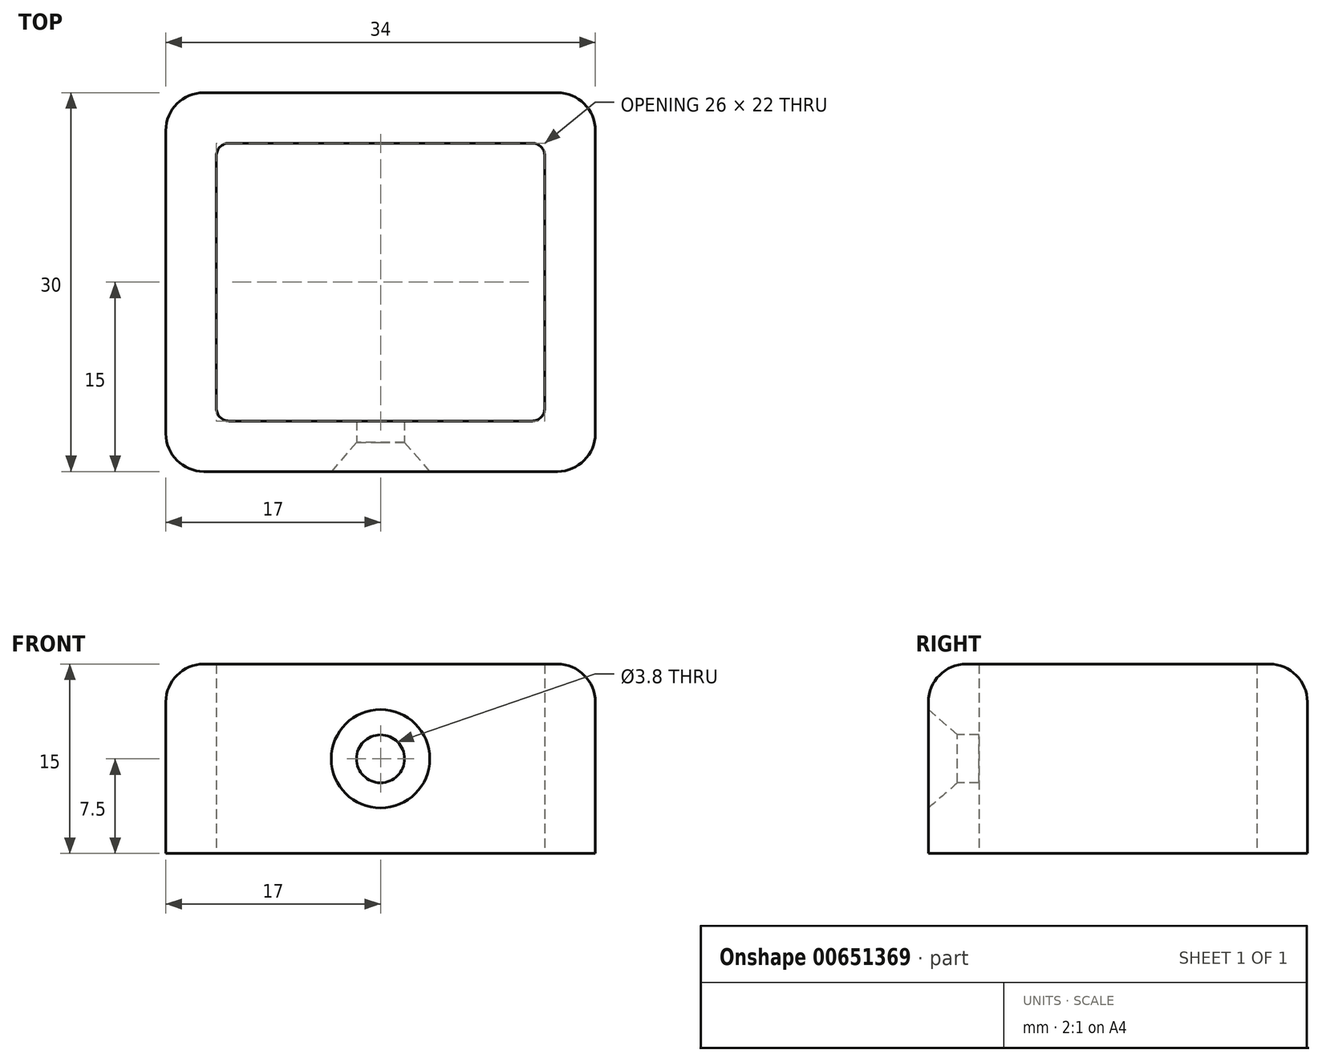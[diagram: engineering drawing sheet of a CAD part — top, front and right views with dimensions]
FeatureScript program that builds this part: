
annotation { "Feature Type Name" : "Feature", "Feature Type Description" : "" }
export const myFeature = defineFeature(function(context is Context, id is Id, definition is map)
    precondition{}
    {
        {
            var Q0;
            Q0=qCreatedBy(makeId("Top.planeOp"),FACE);
            var sketch = newSketch(context, id + "F0", { "sketchPlane" : qUnion([Q0])});
            skLineSegment(sketch, "E0.bottom", {"start": v(13, -11) * mm, "end": v(-13, -11) * mm});
            skLineSegment(sketch, "E0.top", {"start": v(13, 11) * mm, "end": v(-13, 11) * mm});
            skLineSegment(sketch, "E0.left", {"start": v(13, -11) * mm, "end": v(13, 11) * mm});
            skLineSegment(sketch, "E0.right", {"start": v(-13, -11) * mm, "end": v(-13, 11) * mm});
            skPoint(sketch, "E0.middle", {"position": v(0, 0) * mm});
            skLineSegment(sketch, "E1.0", {"start": v(17, 15) * mm, "end": v(-17, 15) * mm});
            skLineSegment(sketch, "E1.1", {"start": v(17, -15) * mm, "end": v(17, 15) * mm});
            skLineSegment(sketch, "E1.2", {"start": v(17, -15) * mm, "end": v(-17, -15) * mm});
            skLineSegment(sketch, "E1.3", {"start": v(-17, -15) * mm, "end": v(-17, 15) * mm});
            skSolve(sketch);
        }
        {
            var Q0;
            Q0=makeQuery(id+"F0.imprint","IMPRINT",FACE,{"disambiguationData":[TD([[makeQuery(id+"F0.imprint","IMPRINT",EDGE,{"derivedFrom":sQuery(id+"F0.wireOp",EDGE,"E0.bottom")}),1.0]])]});
            extrude(context, id + "F1", {"entities" : qUnion([Q0]), "depth" : 15 * mm, "offsetDistance" : 25 * mm});
        }
        {
            var Q0;
            Q0=makeQuery(id+"F1.opExtrude","SWEPT_FACE",FACE,{"disambiguationData":[OSD([sQuery(id+"F0.wireOp",EDGE,"E1.2")])]});
            var sketch = newSketch(context, id + "F2", { "sketchPlane" : qUnion([Q0])});
            skPoint(sketch, "E2", {"position": v(0, 7.5) * mm});
            skPoint(sketch, "E2.positionSnap0", {"position": v(-17, 7.5) * mm});
            skPoint(sketch, "E2.positionSnap1", {"position": v(0, 15) * mm});
            skSolve(sketch);
        }
        {
            var Q0;
            Q0=sQuery(id+"F2.wireOp",VERTEX,"E2");
            var Q1;
            Q1=makeQuery(id+"F1.opExtrude","SWEPT_BODY",BODY,{"disambiguationData":[OSD([sQuery(id+"F0.wireOp",EDGE,"E0.bottom"),sQuery(id+"F0.wireOp",EDGE,"E0.top"),sQuery(id+"F0.wireOp",EDGE,"E0.left"),sQuery(id+"F0.wireOp",EDGE,"E0.right"),sQuery(id+"F0.wireOp",EDGE,"E1.0"),sQuery(id+"F0.wireOp",EDGE,"E1.1"),sQuery(id+"F0.wireOp",EDGE,"E1.2"),sQuery(id+"F0.wireOp",EDGE,"E1.3")])]});
            hole(context, id + "F3", {"style" : HoleStyle.C_SINK, "endStyle" : HoleEndStyle.BLIND, "standardTappedOrClearance" : lookupTablePath({ "standard" : "ANSI", "fit" : "Normal (ASME)", "size" : "#6", "type" : "Clearance" }), "standardBlindInLast" : lookupTablePath({ "fit" : "Free", "standard" : "ANSI", "size" : "#6", "type" : "Clearance" }), "holeDiameter" : 3.8 * mm, "cSinkDiameter" : 7.8 * mm, "cSinkAngle" : 82 * degree, "majorDiameter" : 3.5 * mm, "holeDepth" : 5 * mm, "isTappedThrough" : true, "tappedDepth" : 3.8 * mm, "tapClearance" : 0, "locations" : qUnion([Q0]), "scope" : qUnion([Q1])});
        }
        {
            var Q0;
            Q0=makeQuery(id+"F1.opExtrude","SWEPT_EDGE",EDGE,{"disambiguationData":[OSD([sQuery(id+"F0.wireOp",EDGE,"E1.2"),sQuery(id+"F0.wireOp",EDGE,"E1.3")])]});
            var Q1;
            Q1=makeQuery(id+"F1.opExtrude","SWEPT_EDGE",EDGE,{"disambiguationData":[OSD([sQuery(id+"F0.wireOp",EDGE,"E1.1"),sQuery(id+"F0.wireOp",EDGE,"E1.2")])]});
            var Q2;
            Q2=makeQuery(id+"F1.opExtrude","SWEPT_EDGE",EDGE,{"disambiguationData":[OSD([sQuery(id+"F0.wireOp",EDGE,"E1.0"),sQuery(id+"F0.wireOp",EDGE,"E1.1")])]});
            var Q3;
            Q3=makeQuery(id+"F1.opExtrude","SWEPT_EDGE",EDGE,{"disambiguationData":[OSD([sQuery(id+"F0.wireOp",EDGE,"E1.0"),sQuery(id+"F0.wireOp",EDGE,"E1.3")])]});
            var Q4;
            Q4=makeQuery(id+"F1.opExtrude","CAP_EDGE",EDGE,{"disambiguationData":[OSD([sQuery(id+"F0.wireOp",EDGE,"E1.2")])],"isStart":false});
            var Q5;
            Q5=makeQuery(id+"F1.opExtrude","CAP_EDGE",EDGE,{"disambiguationData":[OSD([sQuery(id+"F0.wireOp",EDGE,"E1.1")])],"isStart":false});
            var Q6;
            Q6=makeQuery(id+"F1.opExtrude","CAP_EDGE",EDGE,{"disambiguationData":[OSD([sQuery(id+"F0.wireOp",EDGE,"E1.0")])],"isStart":false});
            var Q7;
            Q7=makeQuery(id+"F1.opExtrude","CAP_EDGE",EDGE,{"disambiguationData":[OSD([sQuery(id+"F0.wireOp",EDGE,"E1.3")])],"isStart":false});
            fillet(context, id + "F4", {"entities" : qUnion([Q0, Q1, Q2, Q3, Q4, Q5, Q6, Q7]), "radius" : 3 * mm, "tangentPropagation" : true, "allowEdgeOverflow" : false});
        }
        {
            var Q0;
            Q0=makeQuery(id+"F1.opExtrude","SWEPT_EDGE",EDGE,{"disambiguationData":[OSD([sQuery(id+"F0.wireOp",EDGE,"E0.bottom"),sQuery(id+"F0.wireOp",EDGE,"E0.right")])]});
            var Q1;
            Q1=makeQuery(id+"F1.opExtrude","SWEPT_EDGE",EDGE,{"disambiguationData":[OSD([sQuery(id+"F0.wireOp",EDGE,"E0.top"),sQuery(id+"F0.wireOp",EDGE,"E0.right")])]});
            var Q2;
            Q2=makeQuery(id+"F1.opExtrude","SWEPT_EDGE",EDGE,{"disambiguationData":[OSD([sQuery(id+"F0.wireOp",EDGE,"E0.top"),sQuery(id+"F0.wireOp",EDGE,"E0.left")])]});
            var Q3;
            Q3=makeQuery(id+"F1.opExtrude","SWEPT_EDGE",EDGE,{"disambiguationData":[OSD([sQuery(id+"F0.wireOp",EDGE,"E0.bottom"),sQuery(id+"F0.wireOp",EDGE,"E0.left")])]});
            fillet(context, id + "F5", {"entities" : qUnion([Q0, Q1, Q2, Q3]), "radius" : 1 * mm, "tangentPropagation" : true, "allowEdgeOverflow" : false});
        }
    });
